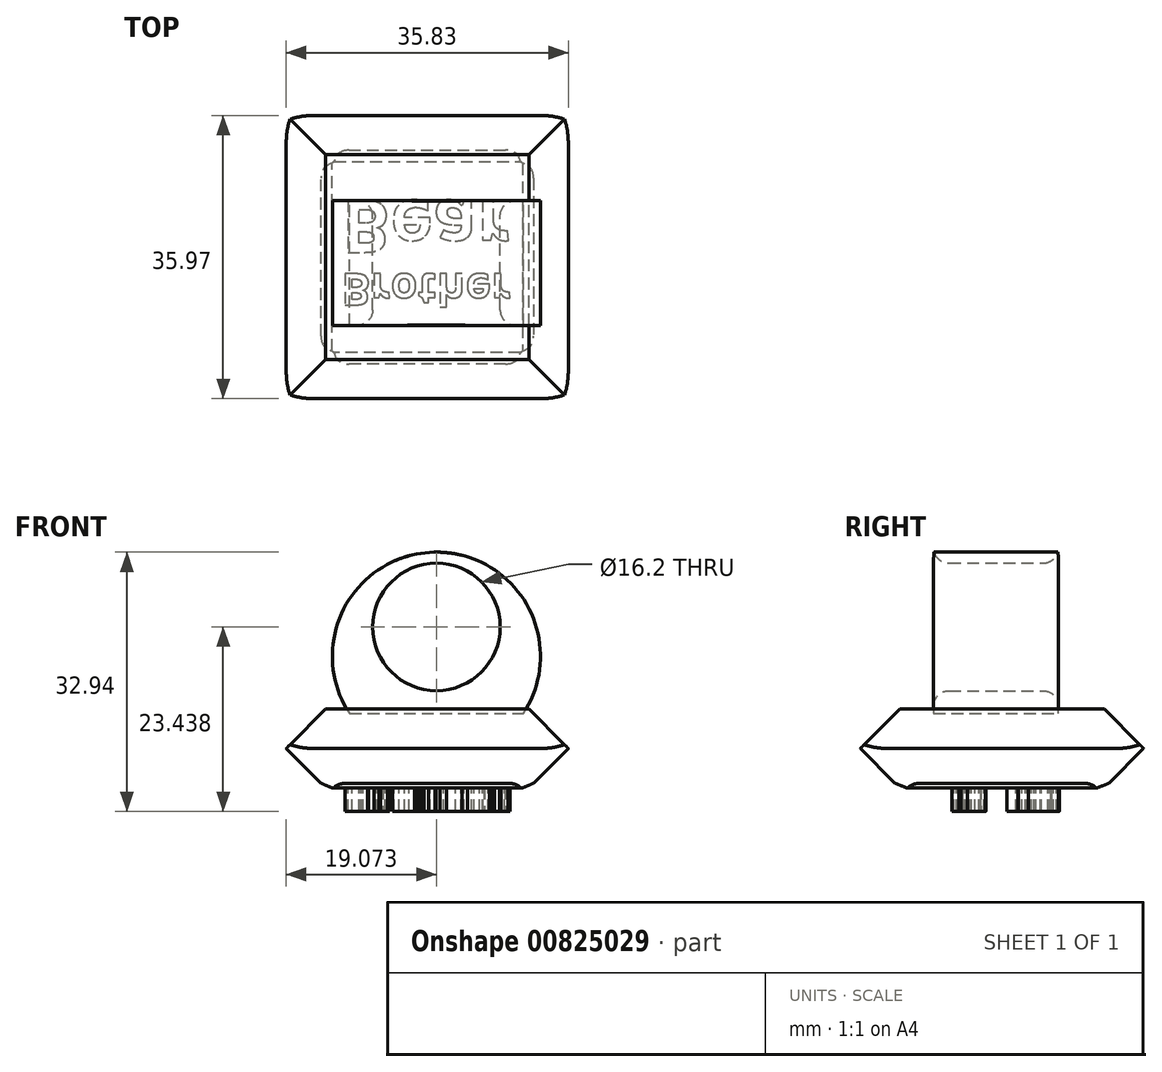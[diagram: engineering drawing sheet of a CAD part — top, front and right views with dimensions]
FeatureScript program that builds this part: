
annotation { "Feature Type Name" : "Feature", "Feature Type Description" : "" }
export const myFeature = defineFeature(function(context is Context, id is Id, definition is map)
    precondition{}
    {
        {
            var Q0;
            Q0=qCreatedBy(makeId("Top.planeOp"),FACE);
            var sketch = newSketch(context, id + "F0", { "sketchPlane" : qUnion([Q0])});
            skLineSegment(sketch, "E0", {"start": v(-35.83, -25.18) * mm, "end": v(0, -25.18) * mm});
            skLineSegment(sketch, "E1", {"start": v(0, -25.18) * mm, "end": v(0, 10.8) * mm});
            skLineSegment(sketch, "E2", {"start": v(0, 10.8) * mm, "end": v(-35.83, 10.8) * mm});
            skLineSegment(sketch, "E3", {"start": v(-35.83, 10.8) * mm, "end": v(-35.83, -25.18) * mm});
            skSolve(sketch);
        }
        {
            var Q0;
            Q0=qSketchRegion(id+"F0",true);
            extrude(context, id + "F1", {"entities" : qUnion([Q0]), "depth" : 10 * mm, "offsetDistance" : 25.4 * mm});
        }
        {
            var Q0;
            Q0=qCreatedBy(makeId("Front.planeOp"),FACE);
            var sketch = newSketch(context, id + "F2", { "sketchPlane" : qUnion([Q0])});
            skLineSegment(sketch, "E4", {"start": v(-30.66, 9.44) * mm, "end": v(-27.8, 9.44) * mm});
            skLineSegment(sketch, "E5", {"start": v(-2.86, 9.44) * mm, "end": v(-5.72, 9.44) * mm});
            skPoint(sketch, "E6.orphan", {"position": v(-33.51, 9.44) * mm});
            skPoint(sketch, "E7.orphan", {"position": v(0, 9.44) * mm});
            skCircle(sketch, "E8", {"center": v(-16.76, 20.44) * mm, "radius": 8.1 * mm});
            skLineSegment(sketch, "E9", {"start": v(-27.8, 9.44) * mm, "end": v(-5.72, 9.44) * mm});
            skArc(sketch, "E10", {"start": v(-5.72, 9.44) * mm, "mid": v(-16.76, 29.94) * mm, "end": v(-27.8, 9.44) * mm});
            skSolve(sketch);
        }
        {
            var Q0;
            Q0=qSketchRegion(id+"F2",true);
            extrude(context, id + "F3", {"entities" : qUnion([Q0]), "depth" : 15.9 * mm, "offsetDistance" : 25 * mm});
        }
        {
            var Q0;
            Q0=makeQuery(id+"F1.opExtrude","CAP_EDGE",EDGE,{"disambiguationData":[OSD([sQuery(id+"F0.wireOp",EDGE,"E0")])],"isStart":true});
            var Q1;
            Q1=makeQuery(id+"F1.opExtrude","CAP_EDGE",EDGE,{"disambiguationData":[OSD([sQuery(id+"F0.wireOp",EDGE,"E3")])],"isStart":false});
            var Q2;
            Q2=makeQuery(id+"F1.opExtrude","CAP_EDGE",EDGE,{"disambiguationData":[OSD([sQuery(id+"F0.wireOp",EDGE,"E0")])],"isStart":false});
            var Q3;
            Q3=makeQuery(id+"F1.opExtrude","CAP_EDGE",EDGE,{"disambiguationData":[OSD([sQuery(id+"F0.wireOp",EDGE,"E3")])],"isStart":true});
            var Q4;
            Q4=makeQuery(id+"F1.opExtrude","CAP_EDGE",EDGE,{"disambiguationData":[OSD([sQuery(id+"F0.wireOp",EDGE,"E2")])],"isStart":false});
            var Q5;
            Q5=makeQuery(id+"F1.opExtrude","CAP_EDGE",EDGE,{"disambiguationData":[OSD([sQuery(id+"F0.wireOp",EDGE,"E2")])],"isStart":true});
            var Q6;
            Q6=makeQuery(id+"F1.opExtrude","CAP_EDGE",EDGE,{"disambiguationData":[OSD([sQuery(id+"F0.wireOp",EDGE,"E1")])],"isStart":false});
            var Q7;
            Q7=makeQuery(id+"F1.opExtrude","CAP_EDGE",EDGE,{"disambiguationData":[OSD([sQuery(id+"F0.wireOp",EDGE,"E1")])],"isStart":true});
            chamfer(context, id + "F4", {"entities" : qUnion([Q0, Q1, Q2, Q3, Q4, Q5, Q6, Q7]), "width" : 5 * mm, "tangentPropagation" : true});
        }
        {
            var Q0;
            {var subQ0=sQuery(id+"F0.wireOp",EDGE,"E3");Q0=makeQuery(id+"F4.opChamfer","BLEND_EDGE",EDGE,{"blendedFrom":[makeQuery(id+"F1.opExtrude","CAP_EDGE",EDGE,{"disambiguationData":[OSD([subQ0])],"isStart":true}),makeQuery(id+"F1.opExtrude","CAP_FACE",FACE,{"disambiguationData":[OSD([sQuery(id+"F0.wireOp",EDGE,"E0"),sQuery(id+"F0.wireOp",EDGE,"E1"),sQuery(id+"F0.wireOp",EDGE,"E2"),subQ0])],"isStart":true})],"blendedInto":[makeQuery(id+"F1.opExtrude","CAP_FACE",FACE,{"disambiguationData":[OSD([sQuery(id+"F0.wireOp",EDGE,"E0"),sQuery(id+"F0.wireOp",EDGE,"E1"),sQuery(id+"F0.wireOp",EDGE,"E2"),subQ0])],"isStart":true})]});}
            var Q1;
            {var subQ0=sQuery(id+"F0.wireOp",EDGE,"E2");Q1=makeQuery(id+"F4.opChamfer","BLEND_EDGE",EDGE,{"blendedFrom":[makeQuery(id+"F1.opExtrude","CAP_EDGE",EDGE,{"disambiguationData":[OSD([subQ0])],"isStart":true}),makeQuery(id+"F1.opExtrude","CAP_FACE",FACE,{"disambiguationData":[OSD([sQuery(id+"F0.wireOp",EDGE,"E0"),sQuery(id+"F0.wireOp",EDGE,"E1"),subQ0,sQuery(id+"F0.wireOp",EDGE,"E3")])],"isStart":true})],"blendedInto":[makeQuery(id+"F1.opExtrude","CAP_FACE",FACE,{"disambiguationData":[OSD([sQuery(id+"F0.wireOp",EDGE,"E0"),sQuery(id+"F0.wireOp",EDGE,"E1"),subQ0,sQuery(id+"F0.wireOp",EDGE,"E3")])],"isStart":true})]});}
            var Q2;
            {var subQ0=sQuery(id+"F0.wireOp",EDGE,"E1");Q2=makeQuery(id+"F4.opChamfer","BLEND_EDGE",EDGE,{"blendedFrom":[makeQuery(id+"F1.opExtrude","CAP_EDGE",EDGE,{"disambiguationData":[OSD([subQ0])],"isStart":true}),makeQuery(id+"F1.opExtrude","CAP_FACE",FACE,{"disambiguationData":[OSD([sQuery(id+"F0.wireOp",EDGE,"E0"),subQ0,sQuery(id+"F0.wireOp",EDGE,"E2"),sQuery(id+"F0.wireOp",EDGE,"E3")])],"isStart":true})],"blendedInto":[makeQuery(id+"F1.opExtrude","CAP_FACE",FACE,{"disambiguationData":[OSD([sQuery(id+"F0.wireOp",EDGE,"E0"),subQ0,sQuery(id+"F0.wireOp",EDGE,"E2"),sQuery(id+"F0.wireOp",EDGE,"E3")])],"isStart":true})]});}
            var Q3;
            {var subQ0=sQuery(id+"F0.wireOp",EDGE,"E0");Q3=makeQuery(id+"F4.opChamfer","BLEND_EDGE",EDGE,{"blendedFrom":[makeQuery(id+"F1.opExtrude","CAP_EDGE",EDGE,{"disambiguationData":[OSD([subQ0])],"isStart":true}),makeQuery(id+"F1.opExtrude","CAP_FACE",FACE,{"disambiguationData":[OSD([subQ0,sQuery(id+"F0.wireOp",EDGE,"E1"),sQuery(id+"F0.wireOp",EDGE,"E2"),sQuery(id+"F0.wireOp",EDGE,"E3")])],"isStart":true})],"blendedInto":[makeQuery(id+"F1.opExtrude","CAP_FACE",FACE,{"disambiguationData":[OSD([subQ0,sQuery(id+"F0.wireOp",EDGE,"E1"),sQuery(id+"F0.wireOp",EDGE,"E2"),sQuery(id+"F0.wireOp",EDGE,"E3")])],"isStart":true})]});}
            chamfer(context, id + "F5", {"entities" : qUnion([Q0, Q1, Q2, Q3]), "width" : 2 * mm, "tangentPropagation" : true});
        }
        {
            var Q0;
            Q0=makeQuery(id+"F1.opExtrude","CAP_FACE",FACE,{"disambiguationData":[OSD([sQuery(id+"F0.wireOp",EDGE,"E0"),sQuery(id+"F0.wireOp",EDGE,"E1"),sQuery(id+"F0.wireOp",EDGE,"E2"),sQuery(id+"F0.wireOp",EDGE,"E3")])],"isStart":true});
            var sketch = newSketch(context, id + "F6", { "sketchPlane" : qUnion([Q0])});
            skText(sketch, "E11", { "text": "Brother", "fontName": "OpenSans-Bold.ttf"});
            skText(sketch, "E12", { "text": "Bear", "fontName": "OpenSans-Bold.ttf"});
            const initialGuessF6  = {"E11": [-0.02883, 0.00932, 1, 0, 0.004], "E12": [-0.02883, 0, 1, 0, 0.00665]};
            skSetInitialGuess(sketch, initialGuessF6);
            skSolve(sketch);
        }
        {
            var Q0;
            Q0 = qSketchRegion(id + "F6", true);
            extrude(context, id + "F7", {"entities" : qUnion([Q0]), "operationType" : NewBodyOperationType.ADD, "depth" : 3 * mm, "offsetDistance" : 25 * mm});
        }
        {
            var Q0;
            Q0=makeQuery(id+"F4.opChamfer","BLEND_EDGE",EDGE,{"blendedFrom":[makeQuery(id+"F1.opExtrude","CAP_EDGE",EDGE,{"disambiguationData":[OSD([sQuery(id+"F0.wireOp",EDGE,"E1")])],"isStart":true}),makeQuery(id+"F1.opExtrude","CAP_EDGE",EDGE,{"disambiguationData":[OSD([sQuery(id+"F0.wireOp",EDGE,"E2")])],"isStart":true})],"blendedInto":[]});
            var Q1;
            Q1=makeQuery(id+"F4.opChamfer","BLEND_EDGE",EDGE,{"blendedFrom":[makeQuery(id+"F1.opExtrude","CAP_EDGE",EDGE,{"disambiguationData":[OSD([sQuery(id+"F0.wireOp",EDGE,"E2")])],"isStart":true}),makeQuery(id+"F1.opExtrude","CAP_EDGE",EDGE,{"disambiguationData":[OSD([sQuery(id+"F0.wireOp",EDGE,"E3")])],"isStart":true})],"blendedInto":[]});
            var Q2;
            Q2=makeQuery(id+"F4.opChamfer","BLEND_EDGE",EDGE,{"blendedFrom":[makeQuery(id+"F1.opExtrude","CAP_EDGE",EDGE,{"disambiguationData":[OSD([sQuery(id+"F0.wireOp",EDGE,"E0")])],"isStart":true}),makeQuery(id+"F1.opExtrude","CAP_EDGE",EDGE,{"disambiguationData":[OSD([sQuery(id+"F0.wireOp",EDGE,"E1")])],"isStart":true})],"blendedInto":[]});
            var Q3;
            Q3=makeQuery(id+"F4.opChamfer","BLEND_EDGE",EDGE,{"blendedFrom":[makeQuery(id+"F1.opExtrude","CAP_EDGE",EDGE,{"disambiguationData":[OSD([sQuery(id+"F0.wireOp",EDGE,"E0")])],"isStart":true}),makeQuery(id+"F1.opExtrude","CAP_EDGE",EDGE,{"disambiguationData":[OSD([sQuery(id+"F0.wireOp",EDGE,"E3")])],"isStart":true})],"blendedInto":[]});
            fillet(context, id + "F8", {"entities" : qUnion([Q0, Q1, Q2, Q3]), "radius" : 5 * mm, "tangentPropagation" : true, "allowEdgeOverflow" : false});
        }
        {
            var Q0;
            Q0=makeQuery(id+"F3.opExtrude","CAP_EDGE",EDGE,{"disambiguationData":[OSD([sQuery(id+"F2.wireOp",EDGE,"E8")])],"isStart":true});
            var Q1;
            Q1=makeQuery(id+"F3.opExtrude","CAP_EDGE",EDGE,{"disambiguationData":[OSD([sQuery(id+"F2.wireOp",EDGE,"E8")])],"isStart":false});
            fillet(context, id + "F9", {"entities" : qUnion([Q0, Q1]), "radius" : 2 * mm, "tangentPropagation" : true, "allowEdgeOverflow" : false});
        }
    });
